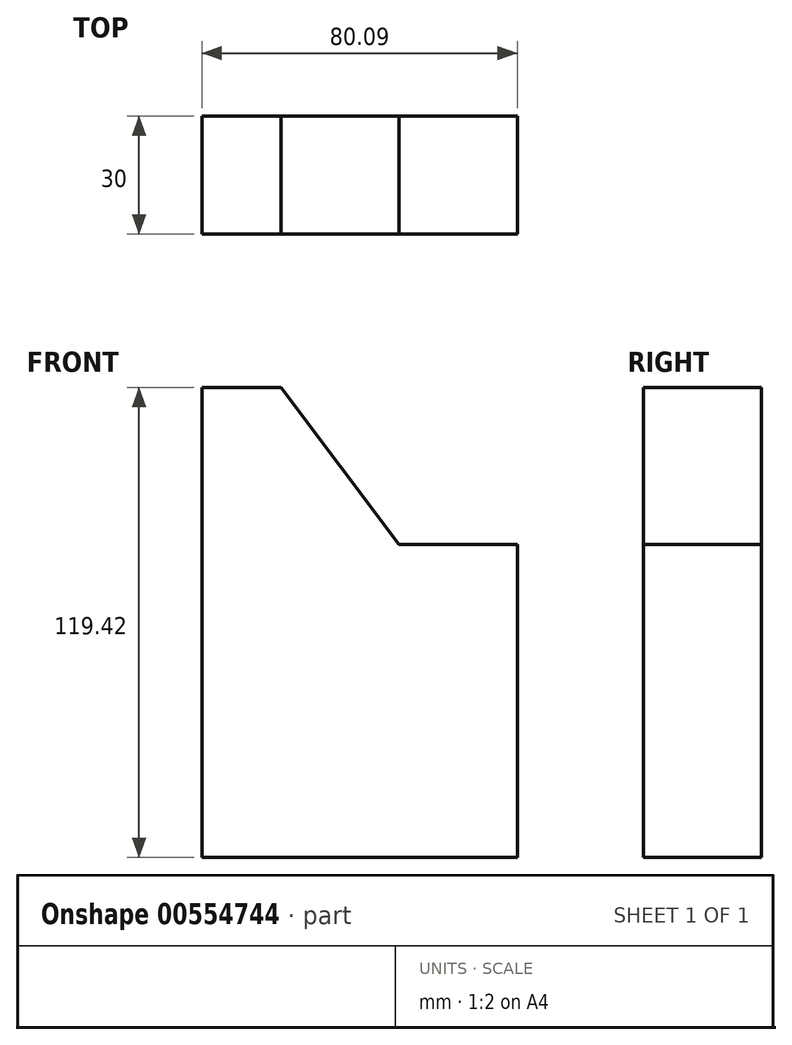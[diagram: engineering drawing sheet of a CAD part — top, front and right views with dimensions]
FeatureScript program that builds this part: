
annotation { "Feature Type Name" : "Feature", "Feature Type Description" : "" }
export const myFeature = defineFeature(function(context is Context, id is Id, definition is map)
    precondition{}
    {
        {
            var Q0;
            Q0=qCreatedBy(makeId("Front.planeOp"),FACE);
            var sketch = newSketch(context, id + "F0", { "sketchPlane" : qUnion([Q0])});
            skLineSegment(sketch, "E0", {"start": v(-68.13, -47.91) * mm, "end": v(11.96, -47.91) * mm});
            skLineSegment(sketch, "E1", {"start": v(-68.13, -47.91) * mm, "end": v(-68.13, 71.51) * mm});
            skLineSegment(sketch, "E2", {"start": v(-68.13, 71.51) * mm, "end": v(-48.13, 71.51) * mm});
            skLineSegment(sketch, "E3", {"start": v(-48.13, 71.51) * mm, "end": v(-18.04, 31.58) * mm});
            skLineSegment(sketch, "E4", {"start": v(11.96, -47.91) * mm, "end": v(11.96, 31.58) * mm});
            skLineSegment(sketch, "E5", {"start": v(11.96, 31.58) * mm, "end": v(-18.04, 31.58) * mm});
            skLineSegment(sketch, "E6", {"start": v(-18.04, 31.58) * mm, "end": v(-34.06, 31.58) * mm, "construction": true});
            skPoint(sketch, "E7.end.orphan", {"position": v(-48.13, 44.03) * mm});
            skLineSegment(sketch, "E8", {"start": v(-48.13, 71.51) * mm, "end": v(-48.13, 44.03) * mm, "construction": true});
            skSolve(sketch);
        }
        {
            var Q0;
            Q0 = qSketchRegion(id + "F0", true);
            extrude(context, id + "F1", {"entities" : qUnion([Q0]), "depth" : 30 * mm, "offsetDistance" : 25 * mm});
        }
    });
